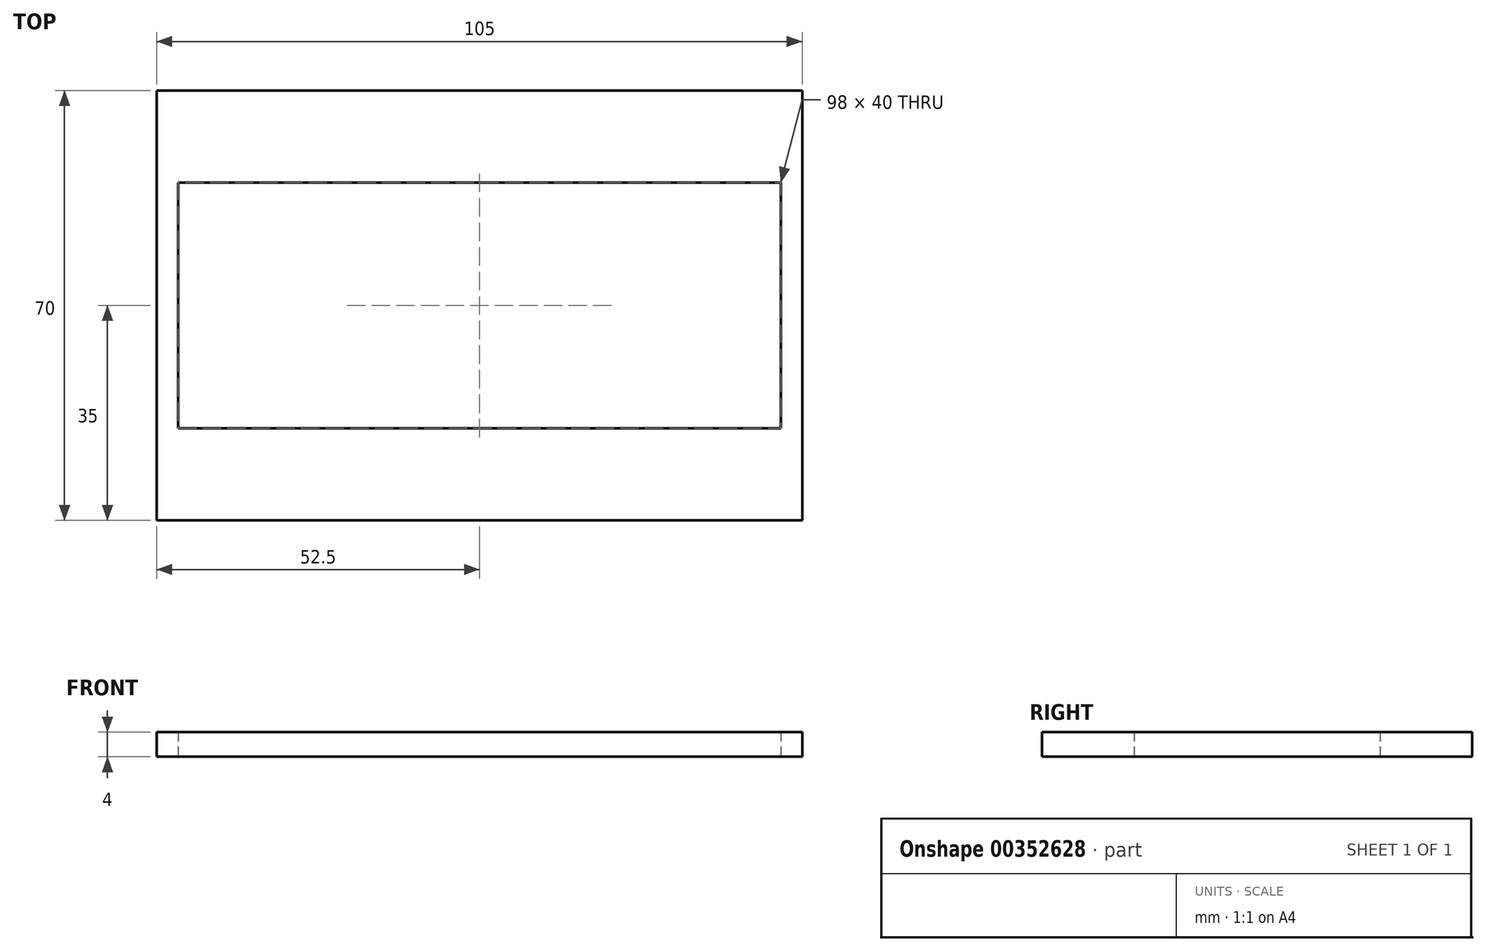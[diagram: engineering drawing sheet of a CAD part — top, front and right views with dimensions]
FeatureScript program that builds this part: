
annotation { "Feature Type Name" : "Feature", "Feature Type Description" : "" }
export const myFeature = defineFeature(function(context is Context, id is Id, definition is map)
    precondition{}
    {
        {
            var Q0;
            Q0=qCreatedBy(makeId("Top.planeOp"),FACE);
            var sketch = newSketch(context, id + "F0", { "sketchPlane" : qUnion([Q0])});
            skLineSegment(sketch, "E0.bottom", {"start": v(-52.5, 35) * mm, "end": v(52.5, 35) * mm});
            skLineSegment(sketch, "E0.top", {"start": v(-52.5, -35) * mm, "end": v(52.5, -35) * mm});
            skLineSegment(sketch, "E0.left", {"start": v(-52.5, 35) * mm, "end": v(-52.5, -35) * mm});
            skLineSegment(sketch, "E0.right", {"start": v(52.5, 35) * mm, "end": v(52.5, -35) * mm});
            skPoint(sketch, "E0.middle", {"position": v(0, 0) * mm});
            skLineSegment(sketch, "E1.bottom", {"start": v(-49, 20) * mm, "end": v(49, 20) * mm});
            skLineSegment(sketch, "E1.top", {"start": v(-49, -20) * mm, "end": v(49, -20) * mm});
            skLineSegment(sketch, "E1.left", {"start": v(-49, 20) * mm, "end": v(-49, -20) * mm});
            skLineSegment(sketch, "E1.right", {"start": v(49, 20) * mm, "end": v(49, -20) * mm});
            skSolve(sketch);
        }
        {
            var Q0;
            Q0 = qSketchRegion(id + "F0", true);
            extrude(context, id + "F1", {"entities" : qUnion([Q0]), "depth" : 4 * mm});
        }
    });
